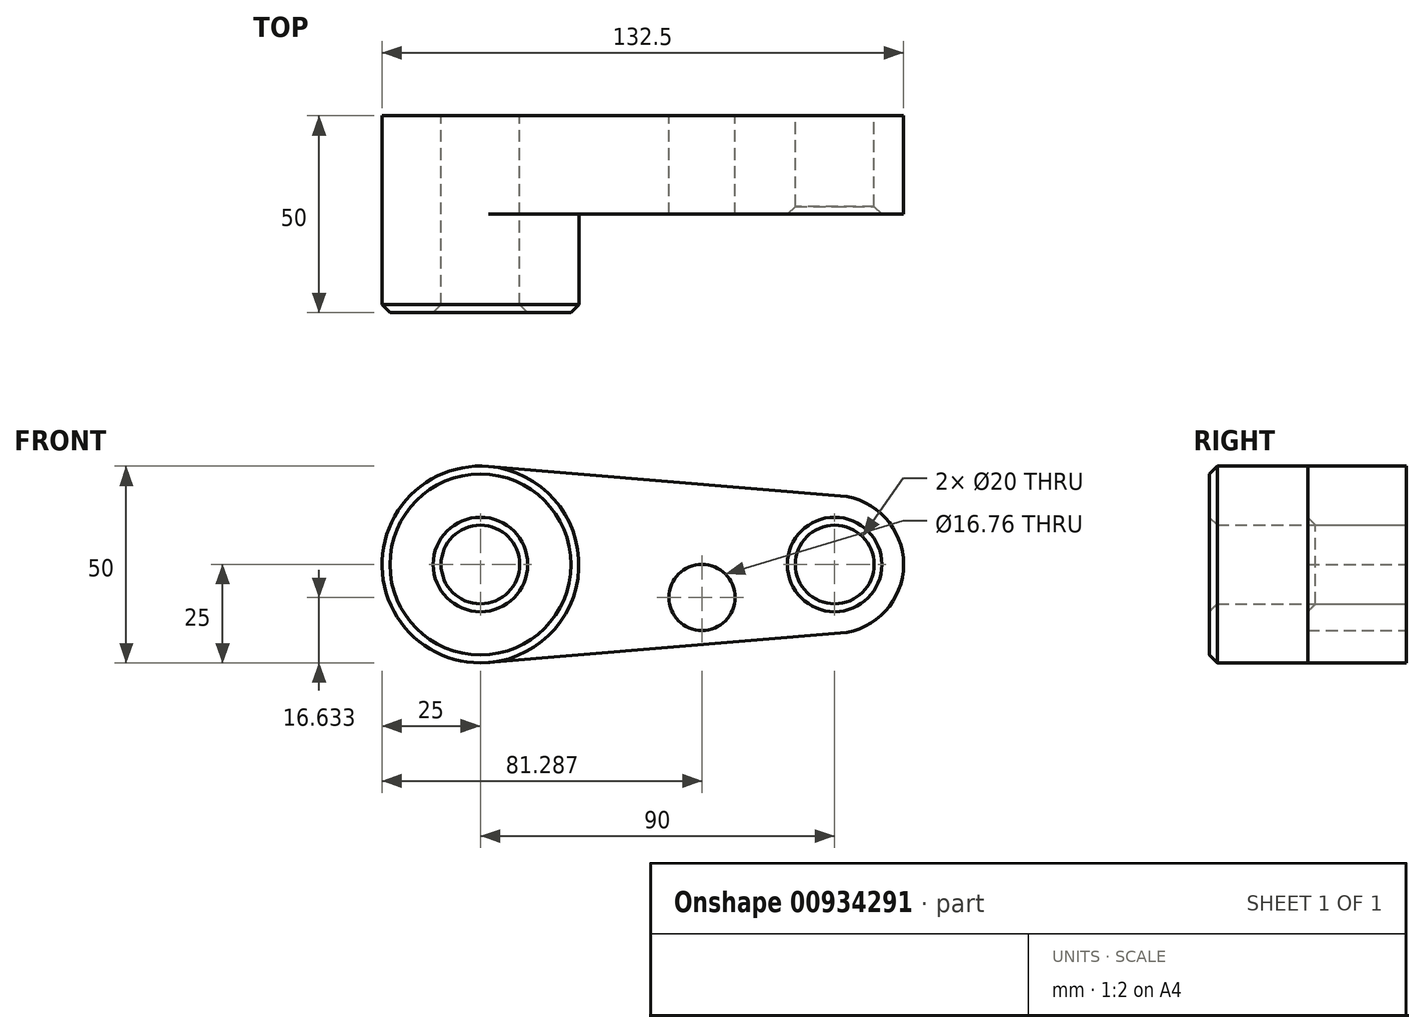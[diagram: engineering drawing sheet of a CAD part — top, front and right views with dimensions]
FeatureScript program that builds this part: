
annotation { "Feature Type Name" : "Feature", "Feature Type Description" : "" }
export const myFeature = defineFeature(function(context is Context, id is Id, definition is map)
    precondition{}
    {
        {
            var Q0;
            Q0=qCreatedBy(makeId("Front.planeOp"),FACE);
            var sketch = newSketch(context, id + "F0", { "sketchPlane" : qUnion([Q0])});
            skCircle(sketch, "E0", {"center": v(0, 0) * mm, "radius": 25 * mm});
            skCircle(sketch, "E1", {"center": v(90, 0) * mm, "radius": 17.5 * mm});
            skLineSegment(sketch, "E2", {"start": v(2.08, 24.91) * mm, "end": v(91.46, 17.44) * mm});
            skLineSegment(sketch, "E3", {"start": v(2.08, -24.91) * mm, "end": v(91.46, -17.44) * mm});
            skCircle(sketch, "E4", {"center": v(0, 0) * mm, "radius": 10 * mm});
            skCircle(sketch, "E5", {"center": v(90, 0) * mm, "radius": 10 * mm});
            skSolve(sketch);
        }
        {
            var Q0;
            Q0=qSketchRegion(id+"F0",true);
            extrude(context, id + "F1", {"entities" : qUnion([Q0]), "depth" : 25 * mm});
        }
        {
            var Q0;
            Q0=makeQuery(id+"F0.imprint","IMPRINT",FACE,{"disambiguationData":[TD([[makeQuery(id+"F0.imprint","IMPRINT",EDGE,{"derivedFrom":sQuery(id+"F0.wireOp",EDGE,"E4")}),-1.0]])]});
            extrude(context, id + "F2", {"entities" : qUnion([Q0]), "operationType" : NewBodyOperationType.ADD, "depth" : 50 * mm});
        }
        {
            var Q0;
            Q0=makeQuery(id+"F2.opExtrude","CAP_EDGE",EDGE,{"disambiguationData":[OSD([sQuery(id+"F0.wireOp",EDGE,"E0")])],"isStart":false});
            var Q1;
            Q1=makeQuery(id+"F2.opExtrude","CAP_EDGE",EDGE,{"disambiguationData":[OSD([sQuery(id+"F0.wireOp",EDGE,"E4")])],"isStart":false});
            var Q2;
            Q2=makeQuery(id+"F1.opExtrude","CAP_EDGE",EDGE,{"disambiguationData":[OSD([sQuery(id+"F0.wireOp",EDGE,"E5")])],"isStart":false});
            chamfer(context, id + "F3", {"entities" : qUnion([Q0, Q1, Q2]), "width" : 2 * mm, "tangentPropagation" : true});
        }
        {
            var Q0;
            Q0=qCreatedBy(makeId("Front.planeOp"),FACE);
            var sketch = newSketch(context, id + "F4", { "sketchPlane" : qUnion([Q0])});
            skCircle(sketch, "E6", {"center": v(56.29, -8.37) * mm, "radius": 8.38 * mm});
            skSolve(sketch);
        }
        {
            var Q0;
            Q0=makeQuery(id+"F4.imprint","IMPRINT",FACE,{"disambiguationData":[TD([[makeQuery(id+"F4.imprint","IMPRINT",EDGE,{"derivedFrom":sQuery(id+"F4.wireOp",EDGE,"E6")}),1.0]])]});
            extrude(context, id + "F5", {"entities" : qUnion([Q0]), "operationType" : NewBodyOperationType.REMOVE, "depth" : 34.2 * mm, "offsetDistance" : 25 * mm});
        }
    });
